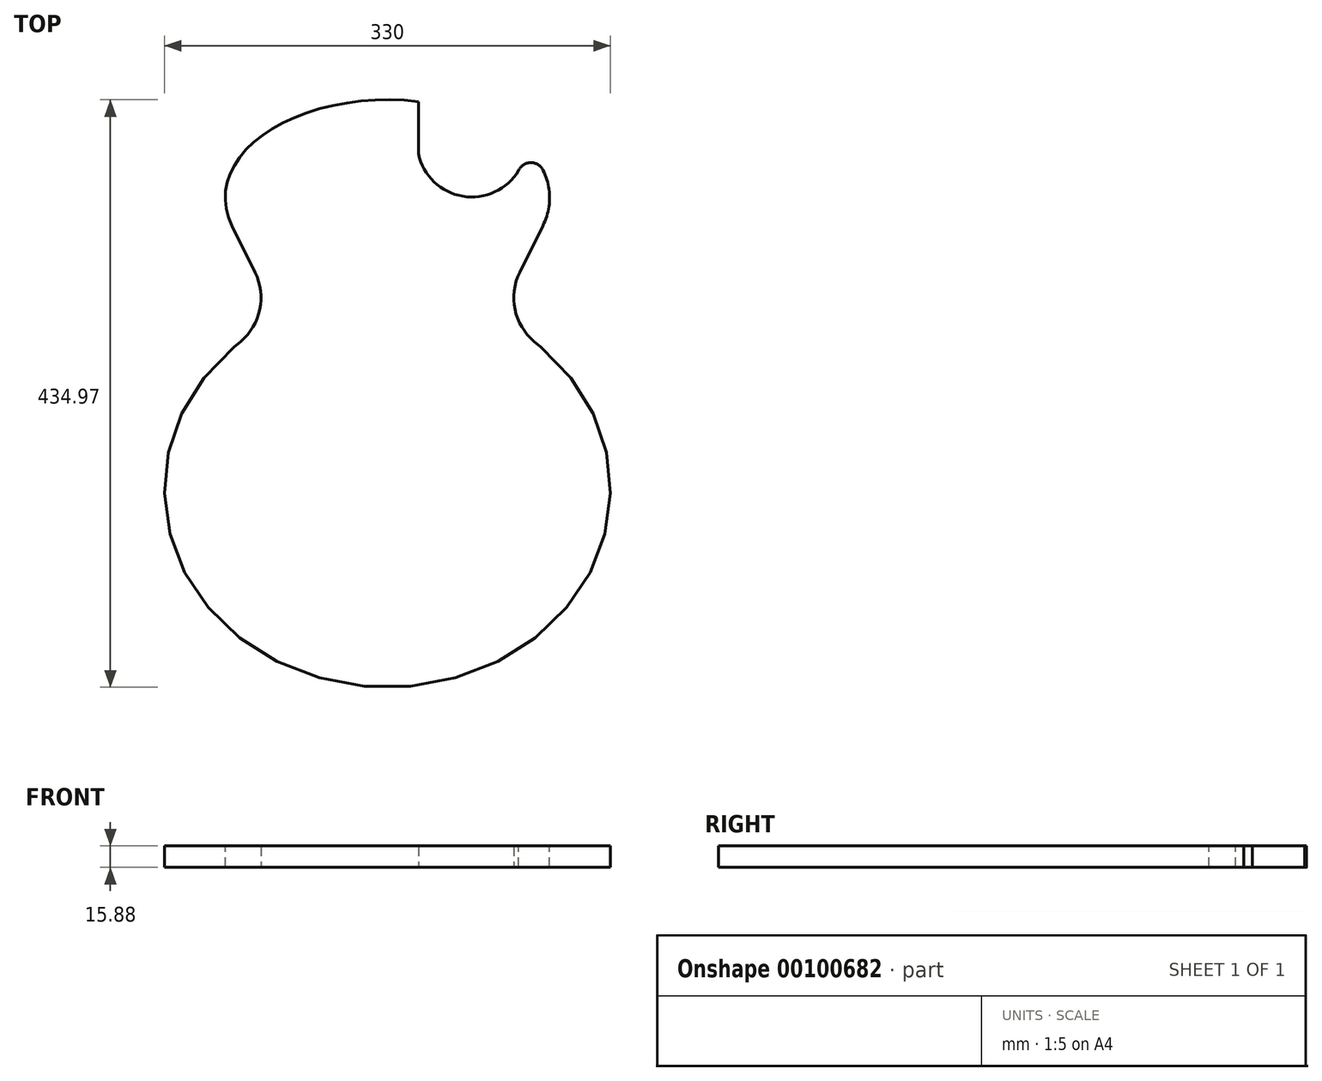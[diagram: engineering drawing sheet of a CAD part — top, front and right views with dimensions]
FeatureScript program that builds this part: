
annotation { "Feature Type Name" : "Feature", "Feature Type Description" : "" }
export const myFeature = defineFeature(function(context is Context, id is Id, definition is map)
    precondition{}
    {
        {
            var Q0;
            Q0=qCreatedBy(makeId("Top.planeOp"),FACE);
            var sketch = newSketch(context, id + "F0", { "sketchPlane" : qUnion([Q0])});
            skEllipticalArc(sketch, "E0", {});
            skEllipticalArc(sketch, "E1", {});
            skLineSegment(sketch, "E2", {"start": v(0, 0) * mm, "end": v(0, 434.98) * mm, "construction": true});
            skLineSegment(sketch, "E3", {"start": v(-244.22, 0) * mm, "end": v(-244.22, 277.4) * mm, "construction": true});
            skLineSegment(sketch, "E4", {"start": v(-244.22, 277.4) * mm, "end": v(0, 277.4) * mm, "construction": true});
            skLineSegment(sketch, "E5", {"start": v(-83.2, 277.4) * mm, "end": v(-113.54, 251.94) * mm, "construction": true});
            skLineSegment(sketch, "E6", {"start": v(-97.86, 307.08) * mm, "end": v(-114.99, 341.74) * mm});
            skArc(sketch, "E7", {"start": v(-108.56, 256.12) * mm, "mid": v(-94.4, 279.75) * mm, "end": v(-97.86, 307.08) * mm});
            skEllipticalArc(sketch, "E8.MirrorCS", {});
            skLineSegment(sketch, "E9.MirrorCS", {"start": v(97.86, 307.08) * mm, "end": v(114.99, 341.74) * mm});
            skArc(sketch, "E10.MirrorCS", {"start": v(108.56, 256.12) * mm, "mid": v(94.4, 279.75) * mm, "end": v(97.86, 307.08) * mm});
            skEllipticalArc(sketch, "E11.MirrorCS", {});
            skPoint(sketch, "E12.orphan", {"position": v(120.66, 353.23) * mm});
            skPoint(sketch, "E13.orphan", {"position": v(-120.66, 353.23) * mm});
            skLineSegment(sketch, "E14", {"start": v(-113.54, 251.94) * mm, "end": v(-108.56, 256.12) * mm});
            skLineSegment(sketch, "E15", {"start": v(108.56, 256.12) * mm, "end": v(113.54, 251.94) * mm});
            const initialGuessF0  = {"E0": [0, 0.146, 0, -1, 0.146, 0.165, 3.900459787077389, 6.283185307179586], "E1": [0, 0.362475, -1, 0, 0.12, 0.0725, 4.71238898038469, 0.290121487978938], "E8.MirrorCS": [0, 0.362475, 1, 0, 0.12, 0.0725, 5.993063819200649, 1.5707963267948966], "E11.MirrorCS": [0, 0.146, 0, -1, 0.146, 0.165, 6.283185307179586, 2.3827255201021975]};
            skSetInitialGuess(sketch, initialGuessF0);
            skSolve(sketch);
        }
        {
            var Q0;
            Q0=qSketchRegion(id+"F0",true);
            extrude(context, id + "F1", {"entities" : qUnion([Q0]), "depth" : 15.88 * mm});
        }
        {
            var Q0;
            Q0=makeQuery(id+"F1.opExtrude","CAP_FACE",FACE,{"disambiguationData":[OSD([sQuery(id+"F0.wireOp",EDGE,"E0"),sQuery(id+"F0.wireOp",EDGE,"E1"),sQuery(id+"F0.wireOp",EDGE,"E6"),sQuery(id+"F0.wireOp",EDGE,"E7"),sQuery(id+"F0.wireOp",EDGE,"E8.MirrorCS"),sQuery(id+"F0.wireOp",EDGE,"E9.MirrorCS"),sQuery(id+"F0.wireOp",EDGE,"E10.MirrorCS"),sQuery(id+"F0.wireOp",EDGE,"E11.MirrorCS"),sQuery(id+"F0.wireOp",EDGE,"E14"),sQuery(id+"F0.wireOp",EDGE,"E15")])],"isStart":false});
            var sketch = newSketch(context, id + "F2", { "sketchPlane" : qUnion([Q0])});
            skLineSegment(sketch, "E16", {"start": v(0, 434.98) * mm, "end": v(0, 369.98) * mm, "construction": true});
            skPoint(sketch, "E16.endSnap0", {"position": v(0, 434.98) * mm});
            skLineSegment(sketch, "E17.0", {"start": v(23, 434.98) * mm, "end": v(23, 394.98) * mm});
            skLineSegment(sketch, "E18", {"start": v(0, 434.98) * mm, "end": v(23, 434.98) * mm, "construction": true});
            skArc(sketch, "E19", {"start": v(115.17, 382.83) * mm, "mid": v(106.01, 388.47) * mm, "end": v(97.04, 382.55) * mm});
            skLineSegment(sketch, "E20", {"start": v(115.17, 382.83) * mm, "end": v(89.92, 434.98) * mm});
            skLineSegment(sketch, "E21", {"start": v(23, 434.98) * mm, "end": v(89.92, 434.98) * mm});
            skLineSegment(sketch, "E22", {"start": v(23, 394.98) * mm, "end": v(23, 362.97) * mm, "construction": true});
            skPoint(sketch, "E23.end.orphan", {"position": v(120, 362.48) * mm});
            skPoint(sketch, "E24.center.orphan", {"position": v(45.5, 394.98) * mm});
            skLineSegment(sketch, "E25", {"start": v(23, 362.98) * mm, "end": v(120, 362.98) * mm, "construction": true});
            skLineSegment(sketch, "E26", {"start": v(120, 362.98) * mm, "end": v(120, 362.98) * mm});
            skArc(sketch, "E27", {"start": v(23, 394.98) * mm, "mid": v(55.78, 363.53) * mm, "end": v(97.04, 382.55) * mm});
            skSolve(sketch);
        }
        {
            var Q0;
            Q0=qSketchRegion(id+"F2",true);
            extrude(context, id + "F3", {"entities" : qUnion([Q0]), "operationType" : NewBodyOperationType.REMOVE, "endBound" : BoundingType.THROUGH_ALL, "oppositeDirection" : true, "depth" : 25 * mm});
        }
        {
            var Q0;
            Q0=qCreatedBy(makeId("Right.planeOp"),FACE);
            var sketch = newSketch(context, id + "F4", { "sketchPlane" : qUnion([Q0])});
            skLineSegment(sketch, "E28", {"start": v(0, 0) * mm, "end": v(0, 4.76) * mm});
            skLineSegment(sketch, "E29", {"start": v(-17.07, 0) * mm, "end": v(-17.07, 3.26) * mm, "construction": true});
            skLineSegment(sketch, "E30", {"start": v(-17.07, 3.26) * mm, "end": v(0, 3.26) * mm, "construction": true});
            skLineSegment(sketch, "E31", {"start": v(0, 3.26) * mm, "end": v(2, 3.26) * mm, "construction": true});
            skLineSegment(sketch, "E32", {"start": v(2, 3.26) * mm, "end": v(39, 3.26) * mm, "construction": true});
            skPoint(sketch, "E33", {"position": v(20.5, 3.26) * mm});
            skLineSegment(sketch, "E34", {"start": v(39, 3.26) * mm, "end": v(39, 4.76) * mm, "construction": true});
            skArc(sketch, "E35", {"start": v(0, 4.76) * mm, "mid": v(19.5, 3.26) * mm, "end": v(39, 4.76) * mm});
            skLineSegment(sketch, "E36", {"start": v(0, 4.76) * mm, "end": v(0, 15.88) * mm});
            skLineSegment(sketch, "E37", {"start": v(0, 15.88) * mm, "end": v(146.13, 15.88) * mm});
            skArc(sketch, "E38", {"start": v(146.13, 15.88) * mm, "mid": v(88.76, 12.72) * mm, "end": v(32.09, 3.26) * mm});
            skLineSegment(sketch, "E39", {"start": v(146.13, 15.88) * mm, "end": v(146.13, -25.51) * mm, "construction": true});
            skSolve(sketch);
        }
    });
